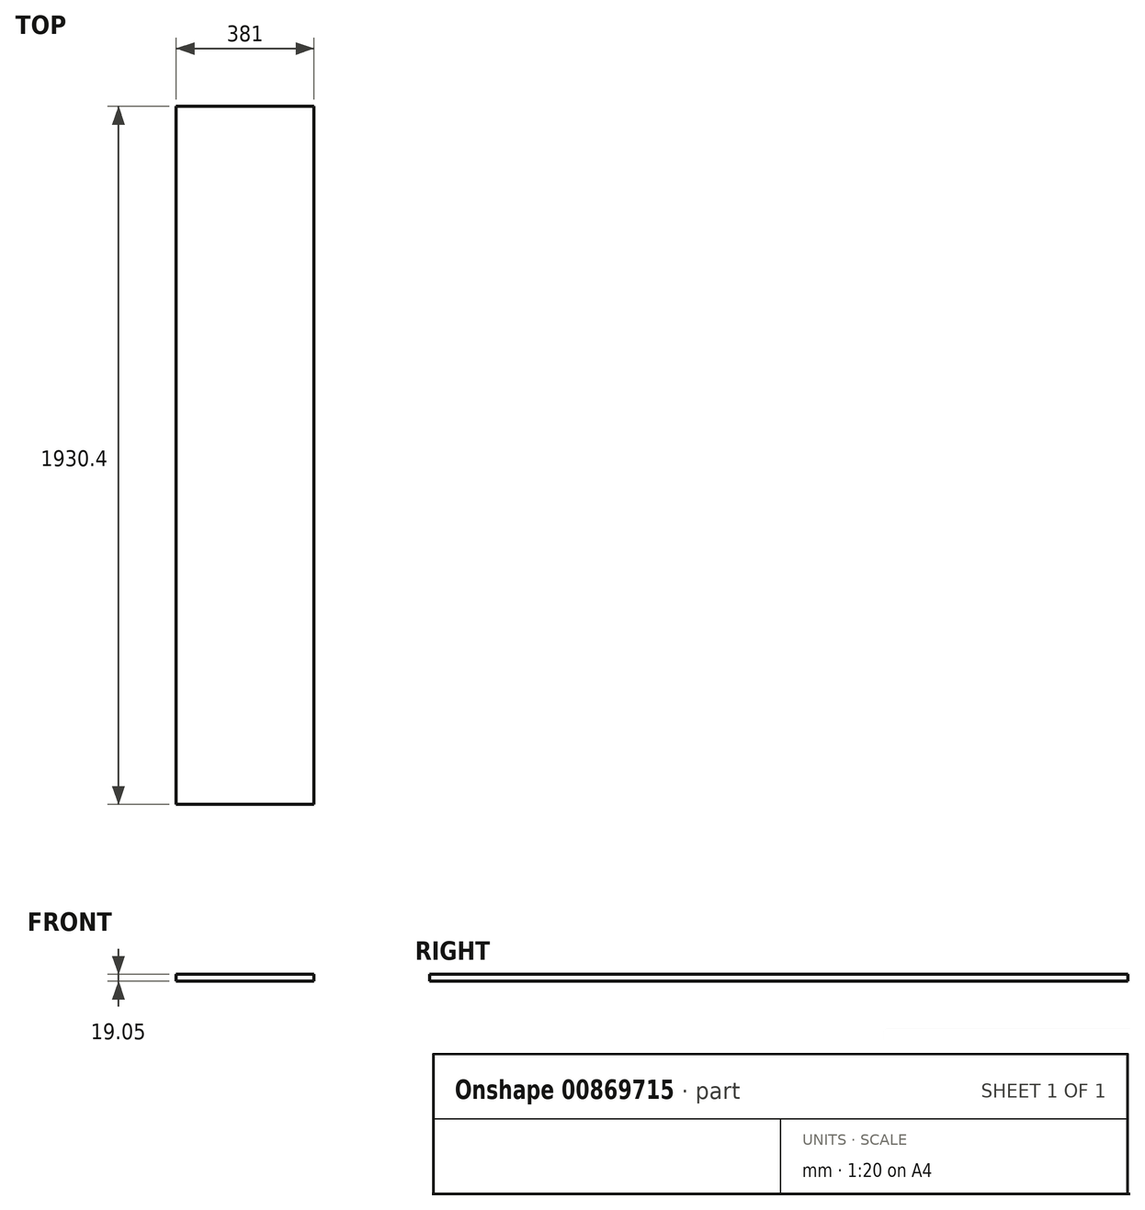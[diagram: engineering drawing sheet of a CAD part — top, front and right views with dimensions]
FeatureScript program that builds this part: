
annotation { "Feature Type Name" : "Feature", "Feature Type Description" : "" }
export const myFeature = defineFeature(function(context is Context, id is Id, definition is map)
    precondition{}
    {
        {
            var Q0;
            Q0=qCreatedBy(makeId("Top.planeOp"),FACE);
            var sketch = newSketch(context, id + "F0", { "sketchPlane" : qUnion([Q0])});
            skLineSegment(sketch, "E0.bottom", {"start": v(0, 0) * mm, "end": v(381, 0) * mm});
            skLineSegment(sketch, "E0.top", {"start": v(0, -1930.4) * mm, "end": v(381, -1930.4) * mm});
            skLineSegment(sketch, "E0.left", {"start": v(0, 0) * mm, "end": v(0, -1930.4) * mm});
            skLineSegment(sketch, "E0.right", {"start": v(381, 0) * mm, "end": v(381, -1930.4) * mm});
            skSolve(sketch);
        }
        {
            var Q0;
            Q0 = qSketchRegion(id + "F0", true);
            extrude(context, id + "F1", {"entities" : qUnion([Q0]), "depth" : 19.05 * mm, "offsetDistance" : 25.4 * mm});
        }
    });
